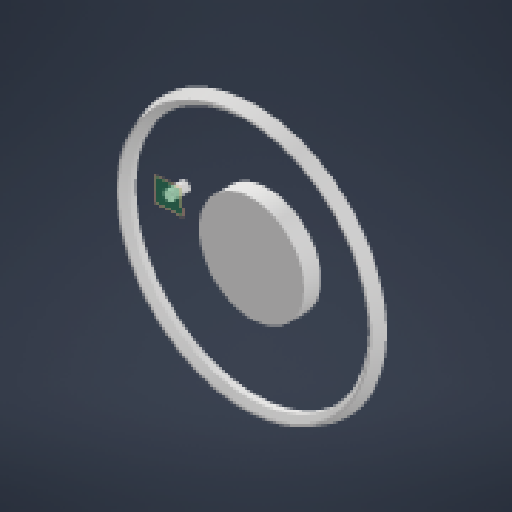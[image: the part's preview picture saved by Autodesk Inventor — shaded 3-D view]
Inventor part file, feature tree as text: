
AUTODESK INVENTOR PART (.ipt)
format: ipt  version: 2024 (Build 280153000, 153)  size: 251,904 bytes
history: native  units: in
note: dims shown in document units (in); Inventor stores cm internally (conversion verified against a paired STEP export)
features: other x7, extrude x2, chamfer x2, sketch x2, reference x2, plane x1
ambient origin geometry x8: Origin, YZ Plane, XZ Plane, XY Plane, X Axis, Y Axis, Z Axis, Center Point
bodies: Solid1 (feature_tree)
feature tree (16):
  other  "{BB8FE430-83BF-418D-8DF9-9B323D3DB9B9}"
  extrude  "Extrusion1"  Depth=0.2756in
  chamfer  "Chamfer1"  Distance=0.2756in
  chamfer  "Chamfer2"  Distance=0.125in Angle=45.0deg
  plane  "Work Plane1"
  extrude  "Extrusion2"  Depth=0.3937in
  other  "Spur Gear Teeth1"
  sketch  "Sketch1"  dims[d0=0.1181in d1=0.2756in d2=0.2756in d3=0.0in d4=0.125in d5=0.125in d6=45.0deg]
  sketch  "Sketch2"  dims[d7=0.2756in d8=0.125in d9=0.1374in d10=0.0079in d11=0.3937in d12=0.0in]
  reference  "Reference1"
  reference  "Reference2"
  other  "Spur Gear2"
  other  "<userpath>\Desktop\Camera_Mount.iam"
  other  "Camera_Mount.iam"
  other  "MG996R:3"
  other  "Camera_Baseplate:1"
